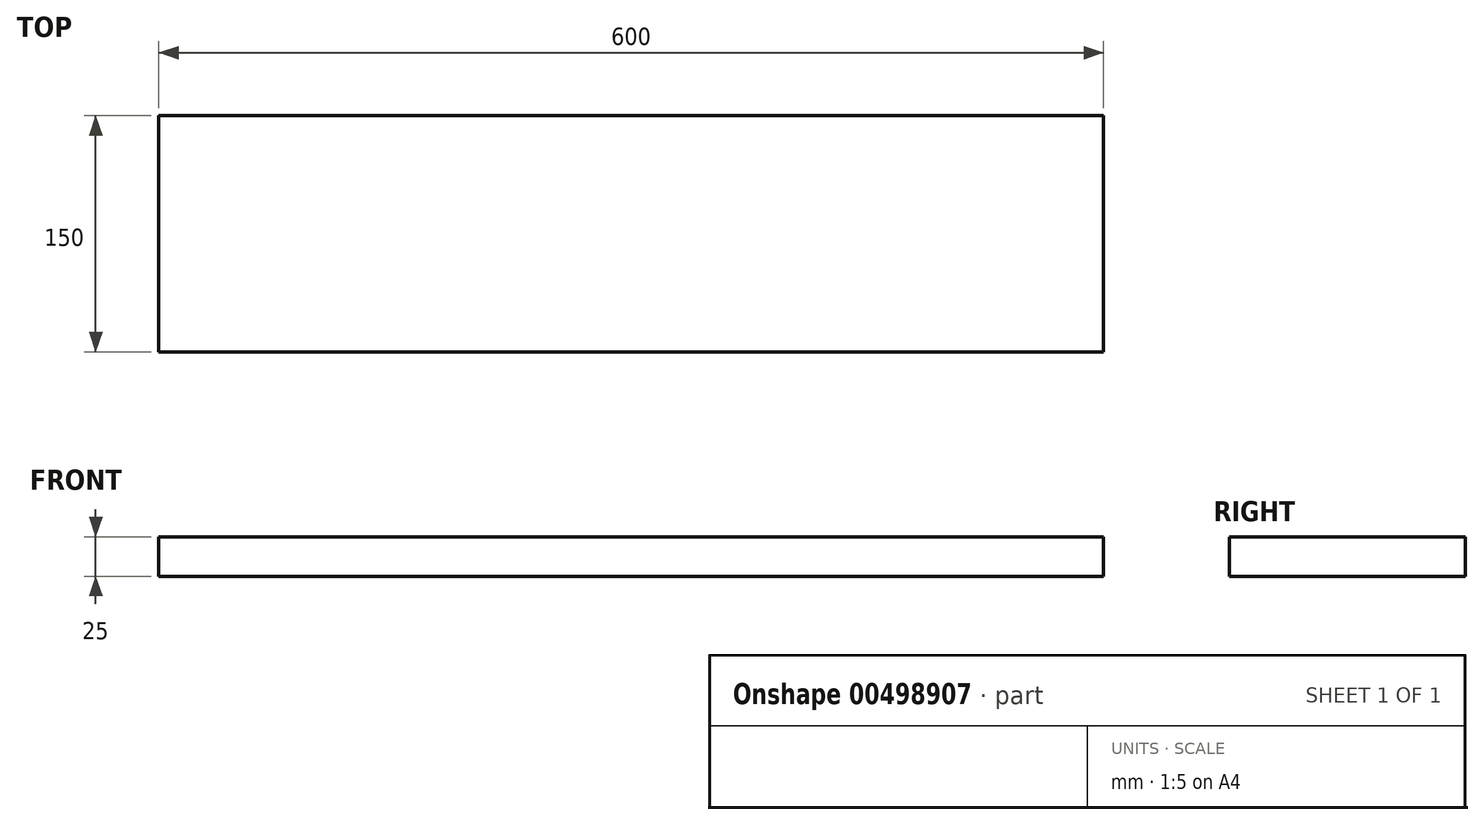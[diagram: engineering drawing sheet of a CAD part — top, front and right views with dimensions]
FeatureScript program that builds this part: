
annotation { "Feature Type Name" : "Feature", "Feature Type Description" : "" }
export const myFeature = defineFeature(function(context is Context, id is Id, definition is map)
    precondition{}
    {
        {
            var Q0;
            Q0=qCreatedBy(makeId("Top.planeOp"),FACE);
            var sketch = newSketch(context, id + "F0", { "sketchPlane" : qUnion([Q0])});
            skLineSegment(sketch, "E0.bottom", {"start": v(-301.42, 33.96) * mm, "end": v(298.58, 33.96) * mm});
            skLineSegment(sketch, "E0.top", {"start": v(-301.42, -116.04) * mm, "end": v(298.58, -116.04) * mm});
            skLineSegment(sketch, "E0.left", {"start": v(-301.42, 33.96) * mm, "end": v(-301.42, -116.04) * mm});
            skLineSegment(sketch, "E0.right", {"start": v(298.58, 33.96) * mm, "end": v(298.58, -116.04) * mm});
            skSolve(sketch);
        }
        {
            var Q0;
            Q0=makeQuery(id+"F0.imprint","IMPRINT",FACE,{"disambiguationData":[TD([[makeQuery(id+"F0.imprint","IMPRINT",EDGE,{"derivedFrom":sQuery(id+"F0.wireOp",EDGE,"E0.bottom")}),-1.0]])]});
            extrude(context, id + "F1", {"entities" : qUnion([Q0]), "depth" : 25 * mm});
        }
    });
